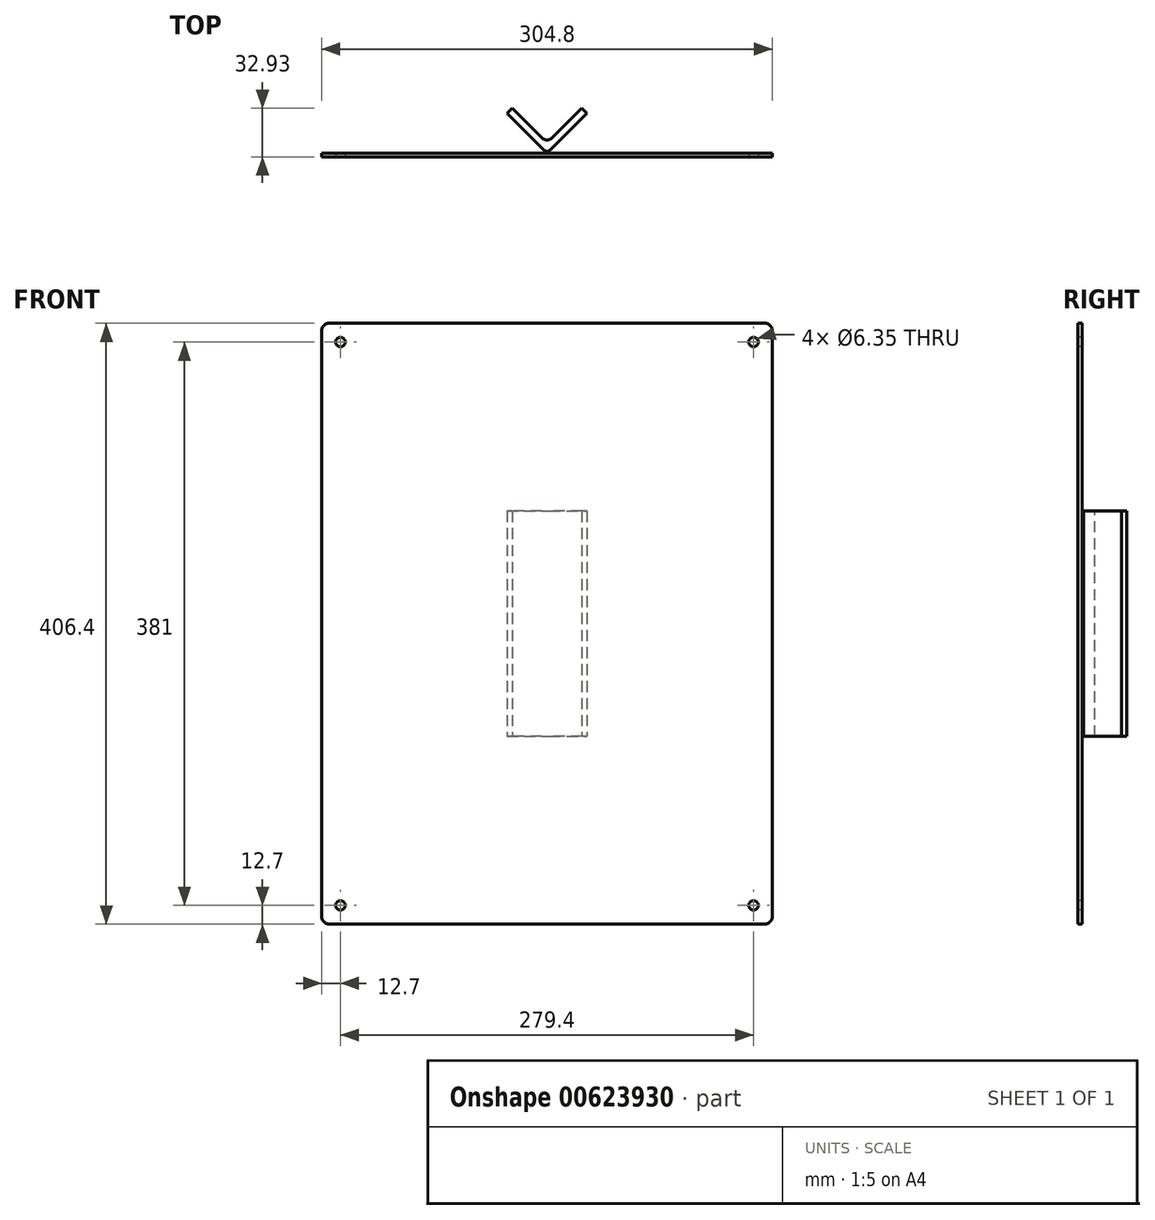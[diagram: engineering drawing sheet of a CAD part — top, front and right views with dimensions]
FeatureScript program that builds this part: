
annotation { "Feature Type Name" : "Feature", "Feature Type Description" : "" }
export const myFeature = defineFeature(function(context is Context, id is Id, definition is map)
    precondition{}
    {
        {
            var Q0;
            Q0=qCreatedBy(makeId("Top.planeOp"),FACE);
            var sketch = newSketch(context, id + "F0", { "sketchPlane" : qUnion([Q0])});
            skLineSegment(sketch, "E0", {"start": v(-26.94, 26.94) * mm, "end": v(0, 0) * mm});
            skLineSegment(sketch, "E1", {"start": v(0, 0) * mm, "end": v(26.94, 26.94) * mm});
            skLineSegment(sketch, "E2", {"start": v(26.94, 26.94) * mm, "end": v(23.57, 30.3) * mm});
            skLineSegment(sketch, "E3", {"start": v(23.57, 30.3) * mm, "end": v(0, 6.74) * mm});
            skLineSegment(sketch, "E4", {"start": v(0, 6.74) * mm, "end": v(-23.57, 30.3) * mm});
            skLineSegment(sketch, "E5", {"start": v(-23.57, 30.3) * mm, "end": v(-26.94, 26.94) * mm});
            skCircle(sketch, "E6", {"center": v(0, 42.66) * mm, "radius": 25.4 * mm, "construction": true});
            skSolve(sketch);
        }
        {
            var Q0;
            Q0=qSketchRegion(id+"F0",true);
            extrude(context, id + "F1", {"entities" : qUnion([Q0]), "depth" : 152.4 * mm, "offsetDistance" : 25.4 * mm});
        }
        {
            var Q0;
            Q0=makeQuery(id+"F1.opExtrude","SWEPT_EDGE",EDGE,{"disambiguationData":[OSD([sQuery(id+"F0.wireOp",EDGE,"E3"),sQuery(id+"F0.wireOp",EDGE,"E4")])]});
            fillet(context, id + "F2", {"entities" : qUnion([Q0]), "radius" : 5.08 * mm, "tangentPropagation" : true, "allowEdgeOverflow" : false});
        }
        {
            var Q0;
            Q0=makeQuery(id+"F1.opExtrude","SWEPT_EDGE",EDGE,{"disambiguationData":[OSD([sQuery(id+"F0.wireOp",EDGE,"E0"),sQuery(id+"F0.wireOp",EDGE,"E1")])]});
            fillet(context, id + "F3", {"entities" : qUnion([Q0]), "radius" : 2.54 * mm, "tangentPropagation" : true, "allowEdgeOverflow" : false});
        }
        {
            var Q0;
            Q0=qCreatedBy(makeId("Front.planeOp"),FACE);
            var sketch = newSketch(context, id + "F4", { "sketchPlane" : qUnion([Q0])});
            skLineSegment(sketch, "E7.bottom", {"start": v(152.4, 279.4) * mm, "end": v(-152.4, 279.4) * mm});
            skLineSegment(sketch, "E7.top", {"start": v(152.4, -127) * mm, "end": v(-152.4, -127) * mm});
            skLineSegment(sketch, "E7.left", {"start": v(152.4, 279.4) * mm, "end": v(152.4, -127) * mm});
            skLineSegment(sketch, "E7.right", {"start": v(-152.4, 279.4) * mm, "end": v(-152.4, -127) * mm});
            skPoint(sketch, "E7.middle", {"position": v(0, 76.2) * mm});
            skLineSegment(sketch, "E8", {"start": v(0, 0) * mm, "end": v(0, 152.4) * mm, "construction": true});
            skSolve(sketch);
        }
        {
            var Q0;
            Q0=qSketchRegion(id+"F4",true);
            extrude(context, id + "F5", {"entities" : qUnion([Q0]), "depth" : 2.62 * mm, "offsetDistance" : 25.4 * mm});
        }
        {
            var Q0;
            Q0=makeQuery(id+"F5.opExtrude","CAP_FACE",FACE,{"disambiguationData":[OSD([sQuery(id+"F4.wireOp",EDGE,"E7.bottom"),sQuery(id+"F4.wireOp",EDGE,"E7.top"),sQuery(id+"F4.wireOp",EDGE,"E7.left"),sQuery(id+"F4.wireOp",EDGE,"E7.right")])],"isStart":false});
            var sketch = newSketch(context, id + "F6", { "sketchPlane" : qUnion([Q0])});
            skLineSegment(sketch, "E9.bottom", {"start": v(-139.7, 266.7) * mm, "end": v(139.7, 266.7) * mm, "construction": true});
            skLineSegment(sketch, "E9.top", {"start": v(-139.7, -114.3) * mm, "end": v(139.7, -114.3) * mm, "construction": true});
            skLineSegment(sketch, "E9.left", {"start": v(-139.7, 266.7) * mm, "end": v(-139.7, -114.3) * mm, "construction": true});
            skLineSegment(sketch, "E9.right", {"start": v(139.7, 266.7) * mm, "end": v(139.7, -114.3) * mm, "construction": true});
            skCircle(sketch, "E10", {"center": v(-139.7, 266.7) * mm, "radius": 3.17 * mm});
            skCircle(sketch, "E11", {"center": v(139.7, 266.7) * mm, "radius": 3.17 * mm});
            skCircle(sketch, "E12", {"center": v(139.7, -114.3) * mm, "radius": 3.17 * mm});
            skCircle(sketch, "E13", {"center": v(-139.7, -114.3) * mm, "radius": 3.17 * mm});
            skSolve(sketch);
        }
        {
            var Q0;
            Q0=qSketchRegion(id+"F6",true);
            extrude(context, id + "F7", {"entities" : qUnion([Q0]), "operationType" : NewBodyOperationType.REMOVE, "endBound" : BoundingType.THROUGH_ALL, "oppositeDirection" : true, "depth" : 25.4 * mm, "offsetDistance" : 25.4 * mm});
        }
        {
            var Q0;
            Q0=makeQuery(id+"F5.opExtrude","SWEPT_EDGE",EDGE,{"disambiguationData":[OSD([sQuery(id+"F4.wireOp",EDGE,"E7.bottom"),sQuery(id+"F4.wireOp",EDGE,"E7.right")])]});
            var Q1;
            Q1=makeQuery(id+"F5.opExtrude","SWEPT_EDGE",EDGE,{"disambiguationData":[OSD([sQuery(id+"F4.wireOp",EDGE,"E7.bottom"),sQuery(id+"F4.wireOp",EDGE,"E7.left")])]});
            var Q2;
            Q2=makeQuery(id+"F5.opExtrude","SWEPT_EDGE",EDGE,{"disambiguationData":[OSD([sQuery(id+"F4.wireOp",EDGE,"E7.top"),sQuery(id+"F4.wireOp",EDGE,"E7.left")])]});
            var Q3;
            Q3=makeQuery(id+"F5.opExtrude","SWEPT_EDGE",EDGE,{"disambiguationData":[OSD([sQuery(id+"F4.wireOp",EDGE,"E7.top"),sQuery(id+"F4.wireOp",EDGE,"E7.right")])]});
            fillet(context, id + "F8", {"entities" : qUnion([Q0, Q1, Q2, Q3]), "radius" : 5.08 * mm, "tangentPropagation" : true, "allowEdgeOverflow" : false});
        }
    });
